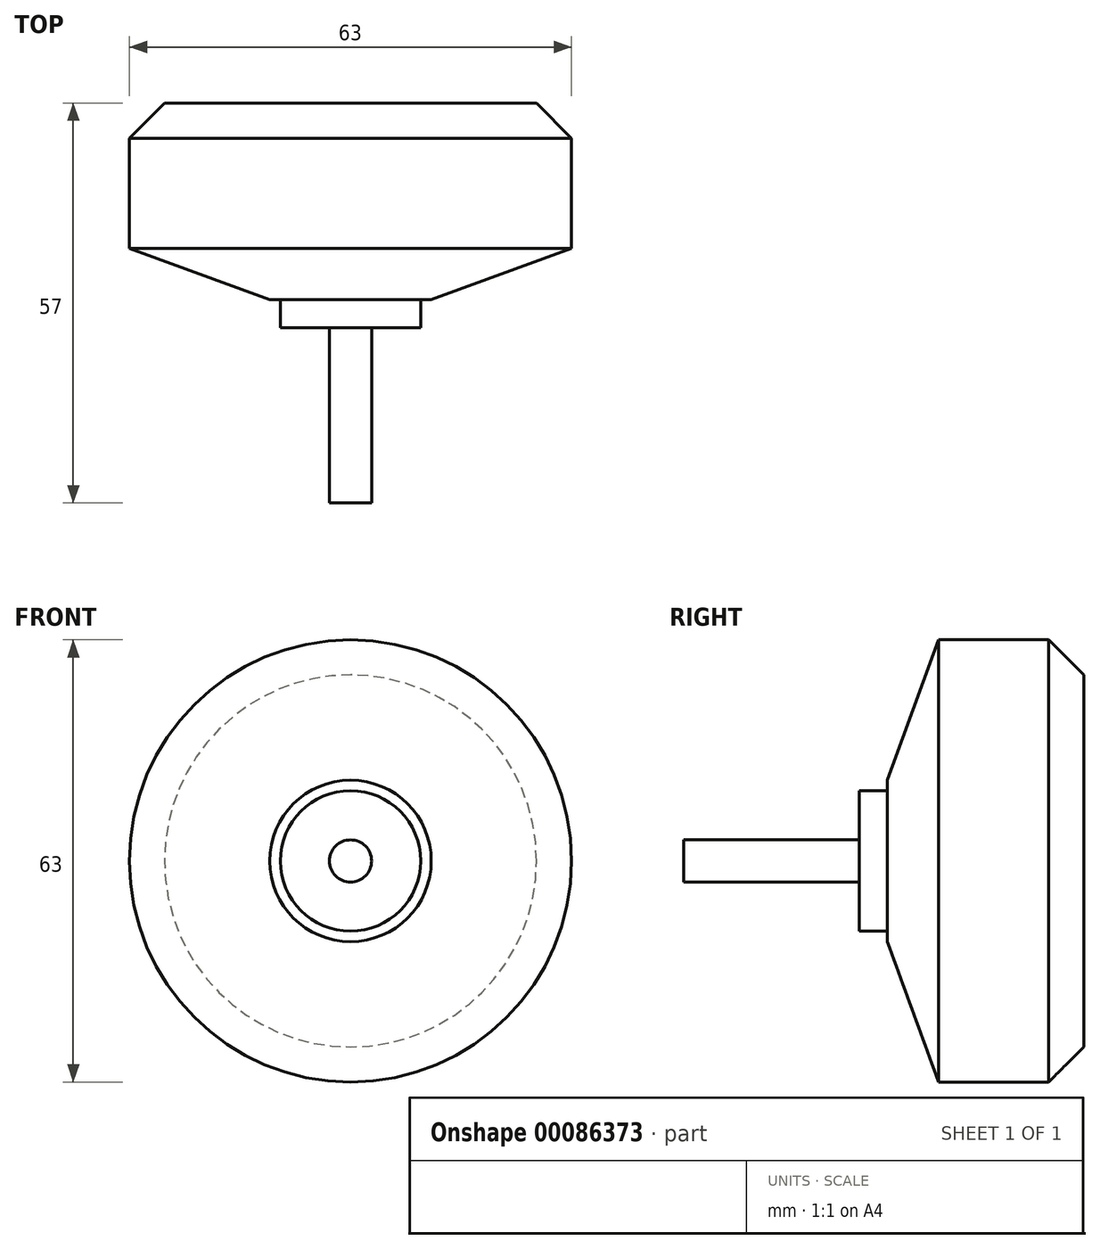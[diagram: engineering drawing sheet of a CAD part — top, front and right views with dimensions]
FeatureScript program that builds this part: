
annotation { "Feature Type Name" : "Feature", "Feature Type Description" : "" }
export const myFeature = defineFeature(function(context is Context, id is Id, definition is map)
    precondition{}
    {
        {
            var Q0;
            Q0=qCreatedBy(makeId("Front.planeOp"),FACE);
            var sketch = newSketch(context, id + "F0", { "sketchPlane" : qUnion([Q0])});
            skCircle(sketch, "E0", {"center": v(0, 0) * mm, "radius": 31.5 * mm});
            skSolve(sketch);
        }
        {
            var Q0;
            Q0 = qSketchRegion(id + "F0", true);
            extrude(context, id + "F1", {"entities" : qUnion([Q0]), "depth" : 28 * mm, "offsetDistance" : 25 * mm});
        }
        {
            var Q0;
            Q0=makeQuery(id+"F1.opExtrude","CAP_FACE",FACE,{"disambiguationData":[OSD([sQuery(id+"F0.wireOp",EDGE,"E0")])],"isStart":false});
            chamfer(context, id + "F2", {"entities" : qUnion([Q0]), "chamferType" : ChamferType.OFFSET_ANGLE, "width" : 20 * mm, "oppositeDirection" : false, "angle" : 20 * degree, "tangentPropagation" : true});
        }
        {
            var Q0;
            Q0=makeQuery(id+"F1.opExtrude","CAP_EDGE",EDGE,{"disambiguationData":[OSD([sQuery(id+"F0.wireOp",EDGE,"E0")])],"isStart":true});
            chamfer(context, id + "F3", {"entities" : qUnion([Q0]), "width" : 5 * mm, "tangentPropagation" : true});
        }
        {
            var Q0;
            Q0=makeQuery(id+"F1.opExtrude","CAP_FACE",FACE,{"disambiguationData":[OSD([sQuery(id+"F0.wireOp",EDGE,"E0")])],"isStart":false});
            var sketch = newSketch(context, id + "F4", { "sketchPlane" : qUnion([Q0])});
            skCircle(sketch, "E1", {"center": v(0, 0) * mm, "radius": 10 * mm});
            skSolve(sketch);
        }
        {
            var Q0;
            Q0 = qSketchRegion(id + "F4", true);
            extrude(context, id + "F5", {"entities" : qUnion([Q0]), "operationType" : NewBodyOperationType.ADD, "depth" : 4 * mm, "offsetDistance" : 25 * mm});
        }
        {
            var Q0;
            Q0=makeQuery(id+"F5.opExtrude","CAP_FACE",FACE,{"disambiguationData":[OSD([sQuery(id+"F4.wireOp",EDGE,"E1")])],"isStart":false});
            var sketch = newSketch(context, id + "F6", { "sketchPlane" : qUnion([Q0])});
            skCircle(sketch, "E2", {"center": v(0, 0) * mm, "radius": 3 * mm});
            skSolve(sketch);
        }
        {
            var Q0;
            Q0 = qSketchRegion(id + "F6", true);
            extrude(context, id + "F7", {"entities" : qUnion([Q0]), "operationType" : NewBodyOperationType.ADD, "depth" : 25 * mm, "offsetDistance" : 25 * mm});
        }
    });
